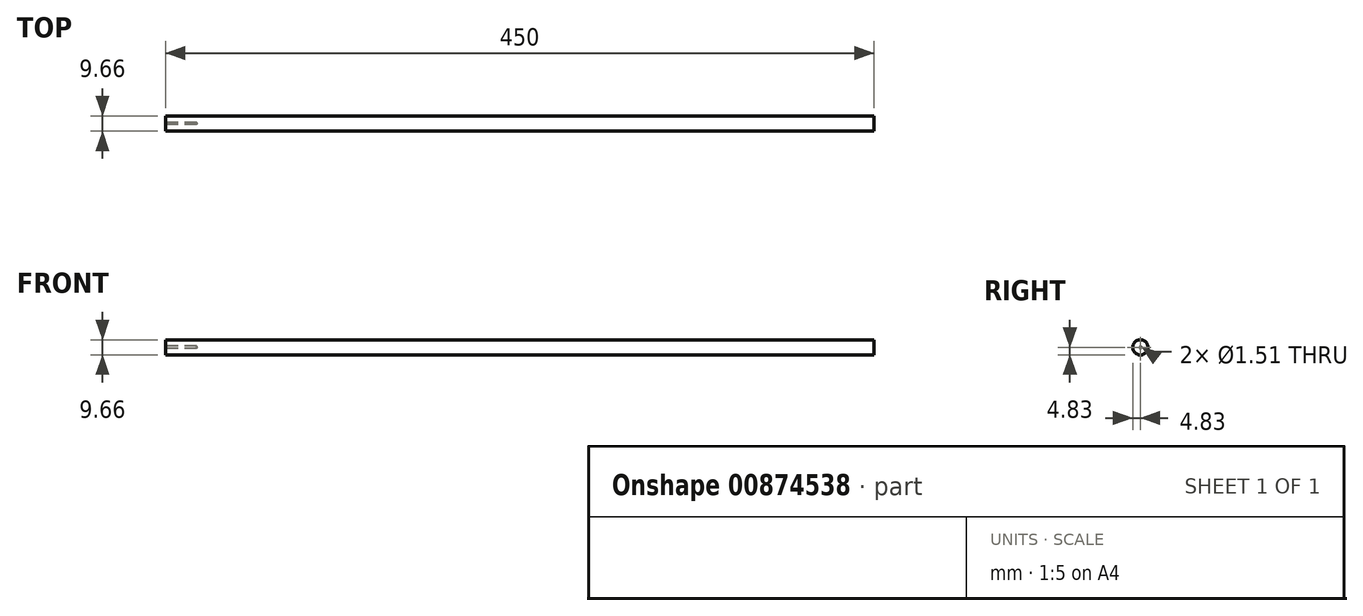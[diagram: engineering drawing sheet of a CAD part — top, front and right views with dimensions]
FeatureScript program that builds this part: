
annotation { "Feature Type Name" : "Feature", "Feature Type Description" : "" }
export const myFeature = defineFeature(function(context is Context, id is Id, definition is map)
    precondition{}
    {
        {
            var Q0;
            Q0=qCreatedBy(makeId("Right.planeOp"),FACE);
            var sketch = newSketch(context, id + "F0", { "sketchPlane" : qUnion([Q0])});
            skCircle(sketch, "E0", {"center": v(0, 0) * mm, "radius": 4.83 * mm});
            skSolve(sketch);
        }
        {
            var Q0;
            Q0=makeQuery(id+"F0.imprint","IMPRINT",FACE,{"disambiguationData":[TD([[makeQuery(id+"F0.imprint","IMPRINT",EDGE,{"derivedFrom":sQuery(id+"F0.wireOp",EDGE,"E0")}),1.0]])]});
            extrude(context, id + "F1", {"entities" : qUnion([Q0]), "depth" : 450 * mm, "offsetDistance" : 25 * mm});
        }
        {
            var Q0;
            Q0=sQuery(id+"F0.wireOp",VERTEX,"E0.center");
            var Q1;
            Q1=sQuery(id+"F0.wireOp",VERTEX,"E0.center");
            var Q2;
            Q2=sQuery(id+"F0.wireOp",VERTEX,"E0.center");
            var Q3;
            Q3=makeQuery(id+"F1.opExtrude","SWEPT_BODY",BODY,{"disambiguationData":[OSD([sQuery(id+"F0.wireOp",EDGE,"E0")])]});
            var Q4;
            Q4=makeQuery(id+"F1.opExtrude","SWEPT_BODY",BODY,{"disambiguationData":[OSD([sQuery(id+"F0.wireOp",EDGE,"E0")])]});
            var Q5;
            Q5=makeQuery(id+"F1.opExtrude","SWEPT_BODY",BODY,{"disambiguationData":[OSD([sQuery(id+"F0.wireOp",EDGE,"E0")])]});
            var Q6;
            Q6=makeQuery(id+"F1.opExtrude","SWEPT_BODY",BODY,{"disambiguationData":[OSD([sQuery(id+"F0.wireOp",EDGE,"E0")])]});
            hole(context, id + "F2", {"style" : HoleStyle.SIMPLE, "endStyle" : HoleEndStyle.BLIND, "oppositeDirection" : true, "standardTappedOrClearance" : lookupTablePath({ "standard" : "ANSI", "engagement" : "75%", "pitch" : "64 tpi", "size" : "#1", "type" : "Tapped" }), "standardBlindInLast" : lookupTablePath({ "standard" : "ANSI", "engagement" : "75%", "pitch" : "64 tpi", "size" : "#1", "type" : "Tapped" }), "holeDiameter" : 1.51 * mm, "majorDiameter" : 1.85 * mm, "showTappedDepth" : true, "holeDepth" : 19.7 * mm, "isTappedThrough" : true, "tappedDepth" : 18.5 * mm, "tapClearance" : 3, "startFromSketch" : true, "locations" : qUnion([Q0, Q1, Q2]), "scope" : qUnion([Q3, Q4, Q5, Q6])});
        }
        {
            var Q0;
            Q0=sQuery(id+"F0.wireOp",VERTEX,"E0.center");
            var Q1;
            Q1=makeQuery(id+"F1.opExtrude","SWEPT_BODY",BODY,{"disambiguationData":[OSD([sQuery(id+"F0.wireOp",EDGE,"E0")])]});
            hole(context, id + "F3", {"style" : HoleStyle.SIMPLE, "endStyle" : HoleEndStyle.BLIND, "standardTappedOrClearance" : lookupTablePath({ "standard" : "ANSI", "engagement" : "75%", "pitch" : "64 tpi", "size" : "#1", "type" : "Tapped" }), "standardBlindInLast" : lookupTablePath({ "standard" : "ANSI", "engagement" : "75%", "pitch" : "64 tpi", "size" : "#1", "type" : "Tapped" }), "holeDiameter" : 1.51 * mm, "majorDiameter" : 1.85 * mm, "showTappedDepth" : true, "holeDepth" : 19.7 * mm, "isTappedThrough" : true, "tappedDepth" : 18.5 * mm, "tapClearance" : 3, "startFromSketch" : true, "locations" : qUnion([Q0]), "scope" : qUnion([Q1])});
        }
    });
